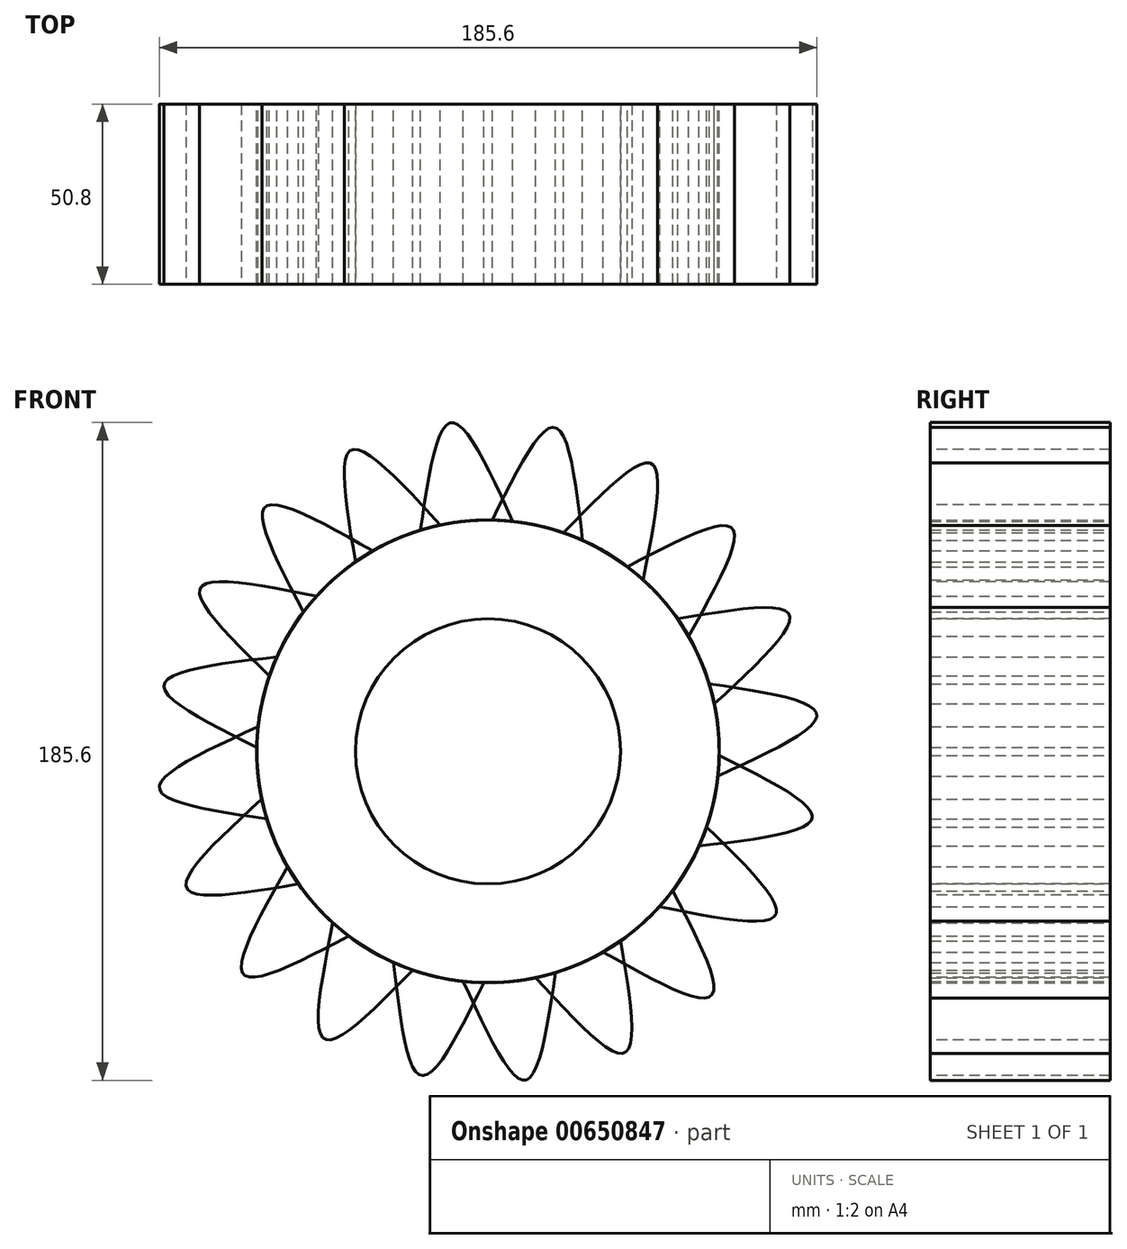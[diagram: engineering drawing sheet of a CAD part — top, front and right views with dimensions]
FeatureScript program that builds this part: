
annotation { "Feature Type Name" : "Feature", "Feature Type Description" : "" }
export const myFeature = defineFeature(function(context is Context, id is Id, definition is map)
    precondition{}
    {
        {
            var Q0;
            Q0=qCreatedBy(makeId("Front.planeOp"),FACE);
            var sketch = newSketch(context, id + "F0", { "sketchPlane" : qUnion([Q0])});
            skCircle(sketch, "E0", {"center": v(0, 0) * mm, "radius": 65.28 * mm});
            skFitSpline(sketch, "E1", {"points": [v(-52.1, 39.33) * mm, v(-62.97, 68.93) * mm, v(-32.52, 56.6) * mm], "startDerivative": vector(-42.44, 80.73) * mm, "endDerivative": vector(81.11, -45.7) * mm});
            skSolve(sketch);
        }
        {
            var Q0;
            {var subQ0=sQuery(id+"F0.wireOp",EDGE,"E1");var subQ1=sQuery(id+"F0.wireOp",EDGE,"E0");var subQ2=makeQuery(id+"F0.imprint","INTERSECT",VERTEX,{"disambiguationData":[OD(0.0)],"derivedFrom":[subQ1,subQ0]});Q0=makeQuery(id+"F0.imprint","IMPRINT",FACE,{"disambiguationData":[TD([[makeQuery(id+"F0.imprint","IMPRINT",EDGE,{"disambiguationData":[TD([[subQ2,1.0]])],"derivedFrom":subQ1}),1.0]])]});}
            var Q1;
            {var subQ0=sQuery(id+"F0.wireOp",EDGE,"E1");Q1=makeQuery(id+"F0.imprint","IMPRINT",FACE,{"disambiguationData":[TD([[makeQuery(id+"F0.imprint","IMPRINT",EDGE,{"derivedFrom":subQ0}),-1.0]])]});}
            extrude(context, id + "F1", {"entities" : qUnion([Q0, Q1]), "depth" : 50.8 * mm, "offsetDistance" : 25.4 * mm});
        }
        {
            var Q0;
            Q0=makeQuery(id+"F1.opExtrude","CAP_FACE",FACE,{"disambiguationData":[OSD([sQuery(id+"F0.wireOp",EDGE,"E0"),sQuery(id+"F0.wireOp",EDGE,"E1")])],"isStart":false});
            var sketch = newSketch(context, id + "F2", { "sketchPlane" : qUnion([Q0])});
            skCircle(sketch, "E2", {"center": v(0, 0) * mm, "radius": 37.4 * mm});
            skSolve(sketch);
        }
        {
            var Q0;
            Q0 = qSketchRegion(id + "F2", true);
            extrude(context, id + "F3", {"entities" : qUnion([Q0]), "operationType" : NewBodyOperationType.REMOVE, "oppositeDirection" : true, "depth" : 131.57 * mm, "offsetDistance" : 25.4 * mm});
        }
        {
            var Q0;
            Q0=makeQuery(id+"F1.opExtrude","SWEPT_BODY",BODY,{"disambiguationData":[OSD([sQuery(id+"F0.wireOp",EDGE,"E0"),sQuery(id+"F0.wireOp",EDGE,"E1")])]});
            var Q1;
            Q1=makeQuery(id+"F1.opExtrude","SWEPT_FACE",FACE,{"disambiguationData":[OSD([sQuery(id+"F0.wireOp",EDGE,"E0")])]});
            circularPattern(context, id + "F4", {"entities" : qUnion([Q0]), "axis" : qUnion([Q1]), "angle" : 360 * degree, "instanceCount" : 20, "equalSpace" : true});
        }
    });
